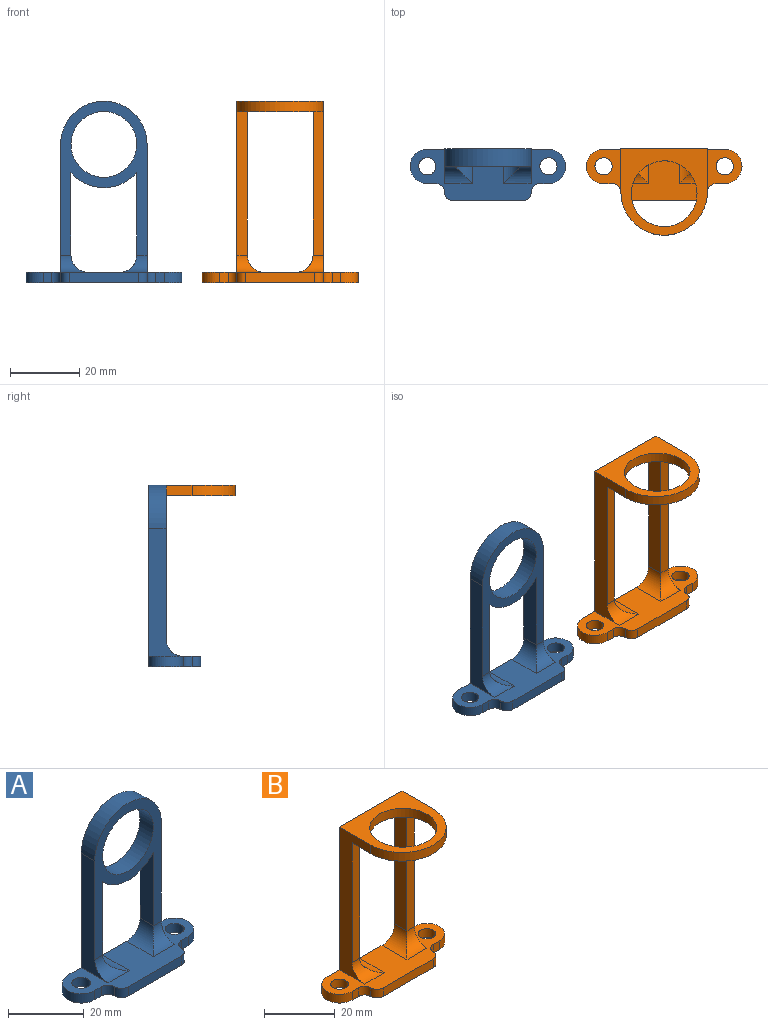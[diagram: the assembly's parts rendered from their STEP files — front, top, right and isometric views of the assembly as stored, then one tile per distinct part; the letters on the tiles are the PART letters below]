
ASSEMBLY  parts=2 mates=2
PART A: 26 faces, bbox 45x15x52.5 mm
  f0: plane 44.5x25mm, normal (0,-1,0), area 366mm2, adj f5,f6,f7,f9,f13,f14,f15,f23
  f1: plane 52.5x35mm, normal (0,1,0), area 511.7mm2, adj f3,f4,f5,f6,f7,f9,f13,f14
  f2: plane 3x2.5mm, normal (0,-1,0), area 7.5mm2, adj f3,f4,f19,f20
  f3: plane 45x15mm, normal (0,0,-1), area 514.3mm2, adj f1,f2,f8,f10,f11,f12,f16,f17
  f4: plane 45x15mm, normal (0,0,1), area 354.3mm2, adj f1,f2,f5,f6,f8,f10,f11,f12
  f5: plane 37x10mm, normal (-1,0,0), area 190.4mm2, adj f0,f1,f4,f9,f24
  f6: plane 37x10mm, normal (1,0,0), area 190.4mm2, adj f0,f1,f4,f9,f23
  f7: cylinder r=9.5mm len=19mm, axis (0,1,0), area 298.5mm2, adj f0,f1
  f8: plane 3x2.5mm, normal (0,-1,0), area 7.5mm2, adj f3,f4,f17,f21
  f9: cylinder r=12.5mm len=25mm, axis (0,1,0), area 196.3mm2, adj f0,f1,f5,f6
  f10: cylinder r=2.5mm len=5mm, axis (0,0,1), area 47.1mm2, adj f3,f4
  f11: cylinder r=2.5mm len=5mm, axis (0,0,1), area 47.1mm2, adj f3,f4
  f12: plane 20x3mm, normal (0,-1,0), area 60mm2, adj f3,f4,f16,f18
  f13: plane 23.88x5mm, normal (-1,0,0), area 119.4mm2, adj f0,f1,f15,f22
  f14: plane 23.88x5mm, normal (1,0,0), area 119.4mm2, adj f0,f1,f15,f25
  f15: cylinder r=12.5mm len=19mm, axis (0,1,0), area 107.9mm2, adj f0,f1,f13,f14
  f16: cylinder r=2.5mm len=3mm, axis (0,0,1), area 11.8mm2, adj f3,f4,f12,f17
  f17: cylinder r=2.5mm len=3mm, axis (0,0,-1), area 11.8mm2, adj f3,f4,f8,f16
  f18: cylinder r=2.5mm len=3mm, axis (0,0,-1), area 11.8mm2, adj f3,f4,f12,f19
  f19: cylinder r=2.5mm len=3mm, axis (0,0,1), area 11.8mm2, adj f2,f3,f4,f18
  f20: cylinder r=5mm len=10mm, axis (0,0,-1), area 47.1mm2, adj f1,f2,f3,f4
  f21: cylinder r=5mm len=10mm, axis (0,0,-1), area 47.1mm2, adj f1,f3,f4,f8
  f22: cylinder r=5mm len=10mm, axis (0,-1,0), area 53.5mm2, adj f1,f4,f13,f23
  f23: cylinder r=5mm len=8mm, axis (1,0,0), area 37.8mm2, adj f0,f4,f6,f22
  f24: cylinder r=5mm len=8mm, axis (1,0,0), area 37.8mm2, adj f0,f4,f5,f25
  f25: cylinder r=5mm len=10mm, axis (0,-1,0), area 53.5mm2, adj f1,f4,f14,f24
PART B: 28 faces, bbox 45x25x52.5 mm
  f0: plane 41.5x5mm, normal (1,0,0), area 207.5mm2, adj f1,f5,f23,f24
  f1: plane 41.5x3mm, normal (0,-1,0), area 124.5mm2, adj f0,f2,f22,f24
  f2: plane 49.5x12.5mm, normal (-1,0,0), area 275.4mm2, adj f1,f5,f8,f22,f24,f25,f27
  f3: plane 49.5x12.5mm, normal (1,0,0), area 275.4mm2, adj f4,f5,f8,f21,f24,f25,f27
  f4: plane 41.5x3mm, normal (0,-1,0), area 124.5mm2, adj f3,f13,f21,f24
  f5: plane 52.5x35mm, normal (0,1,0), area 469.7mm2, adj f0,f2,f3,f7,f8,f13,f18,f19
  f6: plane 3x2.5mm, normal (0,-1,0), area 7.5mm2, adj f7,f8,f17,f18
  f7: plane 45x15mm, normal (0,0,-1), area 514.3mm2, adj f5,f6,f9,f10,f11,f12,f14,f15
  f8: plane 45x15mm, normal (0,0,1), area 354.3mm2, adj f2,f3,f5,f6,f9,f10,f11,f12
  f9: plane 3x2.5mm, normal (0,-1,0), area 7.5mm2, adj f7,f8,f15,f19
  f10: cylinder r=2.5mm len=5mm, axis (0,0,1), area 47.1mm2, adj f7,f8
  f11: cylinder r=2.5mm len=5mm, axis (0,0,1), area 47.1mm2, adj f7,f8
  f12: plane 20x3mm, normal (0,-1,0), area 60mm2, adj f7,f8,f14,f16
  f13: plane 41.5x5mm, normal (-1,0,0), area 207.5mm2, adj f4,f5,f20,f24
  f14: cylinder r=2.5mm len=3mm, axis (0,0,1), area 11.8mm2, adj f7,f8,f12,f15
  f15: cylinder r=2.5mm len=3mm, axis (0,0,-1), area 11.8mm2, adj f7,f8,f9,f14
  f16: cylinder r=2.5mm len=3mm, axis (0,0,-1), area 11.8mm2, adj f7,f8,f12,f17
  f17: cylinder r=2.5mm len=3mm, axis (0,0,1), area 11.8mm2, adj f6,f7,f8,f16
  f18: cylinder r=5mm len=10mm, axis (0,0,-1), area 47.1mm2, adj f5,f6,f7,f8
  f19: cylinder r=5mm len=10mm, axis (0,0,-1), area 47.1mm2, adj f5,f7,f8,f9
  f20: cylinder r=5mm len=10mm, axis (0,-1,0), area 53.5mm2, adj f5,f8,f13,f21
  f21: cylinder r=5mm len=8mm, axis (1,0,0), area 37.8mm2, adj f3,f4,f8,f20
  f22: cylinder r=5mm len=8mm, axis (1,0,0), area 37.8mm2, adj f1,f2,f8,f23
  f23: cylinder r=5mm len=10mm, axis (0,-1,0), area 53.5mm2, adj f0,f5,f8,f22
  f24: plane 25x25mm, normal (0,0,-1), area 244.4mm2, adj f0,f1,f2,f3,f4,f5,f13,f25
  f25: cylinder r=12.5mm len=25mm, axis (0,0,-1), area 117.8mm2, adj f2,f3,f24,f27
  f26: cylinder r=9.5mm len=19mm, axis (0,0,-1), area 179.1mm2, adj f24,f27
  f27: plane 25x25mm, normal (0,0,1), area 274.4mm2, adj f2,f3,f5,f25,f26
PLACE A t=(-20.01,-4.02,4.79)mm
PLACE B t=(30.95,-4.02,4.79)mm
MATE planar B.f7 <-> A.f16  axis (0,0,-1) through (30.95,-10.83,-22.71)mm
MATE planar B.f5 <-> A.f1  axis (0,1,0) through (40.45,-4.02,-14.71)mm
